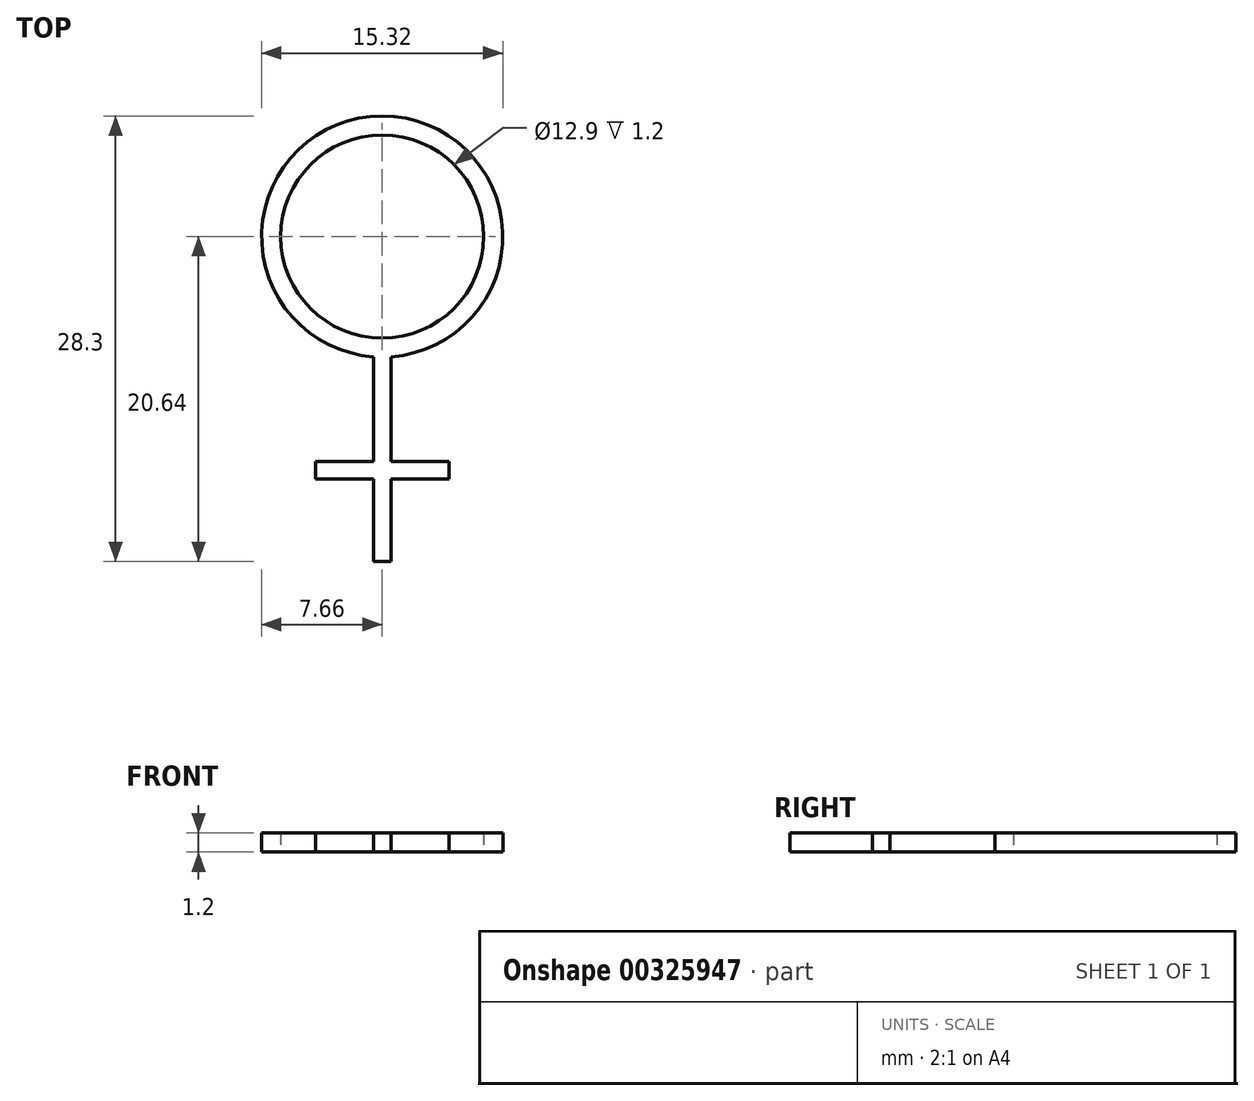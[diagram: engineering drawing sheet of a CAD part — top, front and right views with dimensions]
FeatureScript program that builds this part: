
annotation { "Feature Type Name" : "Feature", "Feature Type Description" : "" }
export const myFeature = defineFeature(function(context is Context, id is Id, definition is map)
    precondition{}
    {
        {
            var Q0;
            Q0=qCreatedBy(makeId("Top.planeOp"),FACE);
            var sketch = newSketch(context, id + "F0", { "sketchPlane" : qUnion([Q0])});
            skArc(sketch, "E0", {"start": v(0.55, -7.64) * mm, "mid": v(0, 7.66) * mm, "end": v(-0.55, -7.64) * mm});
            skCircle(sketch, "E1", {"center": v(0, 0) * mm, "radius": 6.45 * mm});
            skLineSegment(sketch, "E2", {"start": v(-0.55, -15.4) * mm, "end": v(-0.55, -20.64) * mm});
            skLineSegment(sketch, "E3", {"start": v(0.55, -15.4) * mm, "end": v(0.55, -20.64) * mm});
            skLineSegment(sketch, "E4", {"start": v(-0.55, -20.64) * mm, "end": v(0.55, -20.64) * mm});
            skPoint(sketch, "E5.orphan", {"position": v(-0.13, -20.64) * mm});
            skPoint(sketch, "E6.start.orphan", {"position": v(0, 7.66) * mm});
            skPoint(sketch, "E7.oppositeSnap0", {"position": v(0.55, -15.4) * mm});
            skPoint(sketch, "E7.right.end.orphan", {"position": v(5.46, -15.4) * mm});
            skLineSegment(sketch, "E8", {"start": v(-0.55, -7.64) * mm, "end": v(-0.55, -14.3) * mm});
            skLineSegment(sketch, "E9", {"start": v(-0.55, -14.3) * mm, "end": v(-4.23, -14.3) * mm});
            skLineSegment(sketch, "E10", {"start": v(-4.23, -14.3) * mm, "end": v(-4.23, -15.4) * mm});
            skLineSegment(sketch, "E11", {"start": v(-4.23, -15.4) * mm, "end": v(-0.55, -15.4) * mm});
            skLineSegment(sketch, "E12", {"start": v(0.55, -7.64) * mm, "end": v(0.55, -14.3) * mm});
            skLineSegment(sketch, "E13", {"start": v(0.55, -14.3) * mm, "end": v(4.23, -14.3) * mm});
            skLineSegment(sketch, "E14", {"start": v(4.23, -14.3) * mm, "end": v(4.23, -15.4) * mm});
            skLineSegment(sketch, "E15", {"start": v(4.23, -15.4) * mm, "end": v(0.55, -15.4) * mm});
            skSolve(sketch);
        }
        {
            var Q0;
            Q0=makeQuery(id+"F0.imprint","IMPRINT",FACE,{"disambiguationData":[TD([[makeQuery(id+"F0.imprint","IMPRINT",EDGE,{"derivedFrom":sQuery(id+"F0.wireOp",EDGE,"E0")}),1.0]])]});
            extrude(context, id + "F1", {"entities" : qUnion([Q0]), "depth" : 1.2 * mm});
        }
    });
